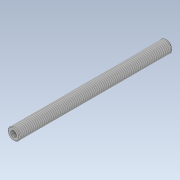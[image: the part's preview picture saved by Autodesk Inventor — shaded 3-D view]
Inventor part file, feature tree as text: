
AUTODESK INVENTOR PART (.ipt)
format: ipt  version: 2021 (Build 250183000, 183)  size: 93,696 bytes
history: native  units: mm
features: other x1, revolve x1, thread x1, chamfer x1, sketch x1
ambient origin geometry x8: Origin, YZ Plane, XZ Plane, XY Plane, X Axis, Y Axis, Z Axis, Center Point
bodies: Body1 (feature_tree)
feature tree (5):
  other  "Sólido1"
  revolve  "Revolución1"  [1 undecoded]
  thread  "Rosca1"  [1 undecoded]
  chamfer  "Chaflán1"  Angle=90.0deg  [1 undecoded]
  sketch  "Boceto1"  dims[d0=129.0mm d1=10.0mm d3=3.0mm d4=90.0deg d5=100.0mm d6=0.0mm d7=0.5mm d8=2.0mm d9=45.0deg]
note: 3 required parameter values undecoded (feature->parameter linkage not recoverable at this tier; creation-order binding heuristic only, values carry confidence <= 0.55)